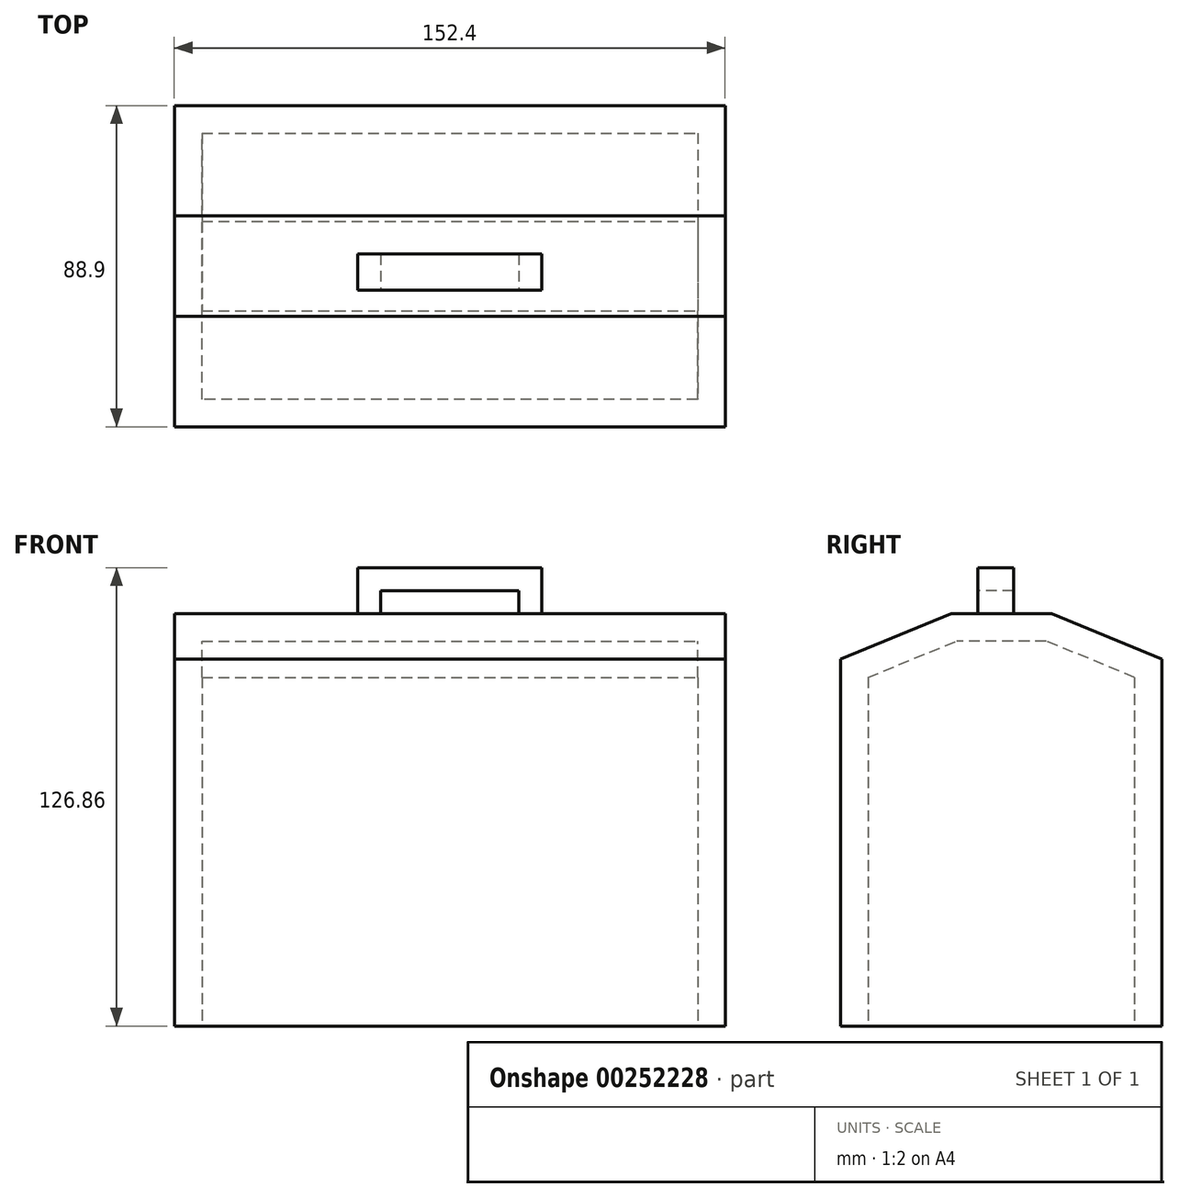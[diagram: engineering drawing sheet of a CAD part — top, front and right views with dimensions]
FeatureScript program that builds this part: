
annotation { "Feature Type Name" : "Feature", "Feature Type Description" : "" }
export const myFeature = defineFeature(function(context is Context, id is Id, definition is map)
    precondition{}
    {
        {
            var Q0;
            Q0=qCreatedBy(makeId("Top.planeOp"),FACE);
            var sketch = newSketch(context, id + "F0", { "sketchPlane" : qUnion([Q0])});
            skLineSegment(sketch, "E0", {"start": v(-77.38, 43.49) * mm, "end": v(75.02, 43.49) * mm});
            skLineSegment(sketch, "E1", {"start": v(75.02, 43.49) * mm, "end": v(75.02, -45.41) * mm});
            skLineSegment(sketch, "E2", {"start": v(75.02, -45.41) * mm, "end": v(-77.38, -45.41) * mm});
            skLineSegment(sketch, "E3", {"start": v(-77.38, -45.41) * mm, "end": v(-77.38, 43.49) * mm});
            skSolve(sketch);
        }
        {
            var Q0;
            Q0=makeQuery(id+"F0.imprint","IMPRINT",FACE,{"disambiguationData":[TD([[makeQuery(id+"F0.imprint","IMPRINT",EDGE,{"derivedFrom":sQuery(id+"F0.wireOp",EDGE,"E0")}),-1.0]])]});
            extrude(context, id + "F1", {"entities" : qUnion([Q0]), "depth" : 101.6 * mm});
        }
        {
            var Q0;
            Q0=makeQuery(id+"F1.opExtrude","SWEPT_FACE",FACE,{"disambiguationData":[OSD([sQuery(id+"F0.wireOp",EDGE,"E1")])]});
            var sketch = newSketch(context, id + "F2", { "sketchPlane" : qUnion([Q0])});
            skLineSegment(sketch, "E4", {"start": v(-45.41, 101.6) * mm, "end": v(-14.87, 114.16) * mm});
            skPoint(sketch, "E5.end.orphan", {"position": v(12.36, 114.16) * mm});
            skLineSegment(sketch, "E6", {"start": v(43.49, 101.6) * mm, "end": v(12.95, 114.16) * mm});
            skLineSegment(sketch, "E7", {"start": v(12.95, 114.16) * mm, "end": v(-14.87, 114.16) * mm});
            skSolve(sketch);
        }
        {
            var Q0;
            Q0=makeQuery(id+"F2.imprint","IMPRINT",FACE,{"disambiguationData":[TD([[makeQuery(id+"F2.imprint","IMPRINT",EDGE,{"derivedFrom":sQuery(id+"F2.wireOp",EDGE,"E4")}),-1.0]])]});
            extrude(context, id + "F3", {"entities" : qUnion([Q0]), "operationType" : NewBodyOperationType.ADD, "oppositeDirection" : true, "depth" : 152.4 * mm});
        }
        {
            var Q0;
            Q0=makeQuery(id+"F3.opExtrude","SWEPT_FACE",FACE,{"disambiguationData":[OSD([sQuery(id+"F2.wireOp",EDGE,"E7")])]});
            var sketch = newSketch(context, id + "F4", { "sketchPlane" : qUnion([Q0])});
            skLineSegment(sketch, "E8", {"start": v(-26.58, 2.38) * mm, "end": v(24.22, 2.38) * mm});
            skLineSegment(sketch, "E9", {"start": v(24.22, 2.38) * mm, "end": v(24.22, -7.55) * mm});
            skLineSegment(sketch, "E10", {"start": v(24.22, -7.55) * mm, "end": v(-26.58, -7.55) * mm});
            skLineSegment(sketch, "E11", {"start": v(-26.58, -7.55) * mm, "end": v(-26.58, 2.38) * mm});
            skSolve(sketch);
        }
        {
            var Q0;
            Q0=makeQuery(id+"F4.imprint","IMPRINT",FACE,{"disambiguationData":[TD([[makeQuery(id+"F4.imprint","IMPRINT",EDGE,{"derivedFrom":sQuery(id+"F4.wireOp",EDGE,"E8")}),-1.0]])]});
            extrude(context, id + "F5", {"entities" : qUnion([Q0]), "operationType" : NewBodyOperationType.ADD, "depth" : 12.7 * mm});
        }
        {
            var Q0;
            Q0=makeQuery(id+"F5.opExtrude","SWEPT_FACE",FACE,{"disambiguationData":[OSD([sQuery(id+"F4.wireOp",EDGE,"E10")])]});
            var sketch = newSketch(context, id + "F6", { "sketchPlane" : qUnion([Q0])});
            skLineSegment(sketch, "E12", {"start": v(-20.23, 120.5) * mm, "end": v(17.87, 120.5) * mm});
            skPoint(sketch, "E12.endSnap0", {"position": v(24.22, 120.5) * mm});
            skLineSegment(sketch, "E13", {"start": v(17.87, 120.5) * mm, "end": v(17.87, 114.16) * mm});
            skLineSegment(sketch, "E14", {"start": v(17.87, 114.16) * mm, "end": v(-20.23, 114.16) * mm});
            skLineSegment(sketch, "E15", {"start": v(-20.23, 114.16) * mm, "end": v(-20.23, 120.5) * mm});
            skPoint(sketch, "E16.start.orphan", {"position": v(-26.58, 120.5) * mm});
            skSolve(sketch);
        }
        {
            var Q0;
            Q0=makeQuery(id+"F6.imprint","IMPRINT",FACE,{"disambiguationData":[TD([[makeQuery(id+"F6.imprint","IMPRINT",EDGE,{"derivedFrom":sQuery(id+"F6.wireOp",EDGE,"E12")}),-1.0]])]});
            extrude(context, id + "F7", {"entities" : qUnion([Q0]), "operationType" : NewBodyOperationType.REMOVE, "oppositeDirection" : true, "depth" : 25.4 * mm});
        }
        {
            var Q0;
            Q0=makeQuery(id+"F1.opExtrude","CAP_FACE",FACE,{"disambiguationData":[OSD([sQuery(id+"F0.wireOp",EDGE,"E0"),sQuery(id+"F0.wireOp",EDGE,"E1"),sQuery(id+"F0.wireOp",EDGE,"E2"),sQuery(id+"F0.wireOp",EDGE,"E3")])],"isStart":true});
            shell(context, id + "F8", {"entities" : qUnion([Q0]), "thickness" : 7.62 * mm});
        }
    });
